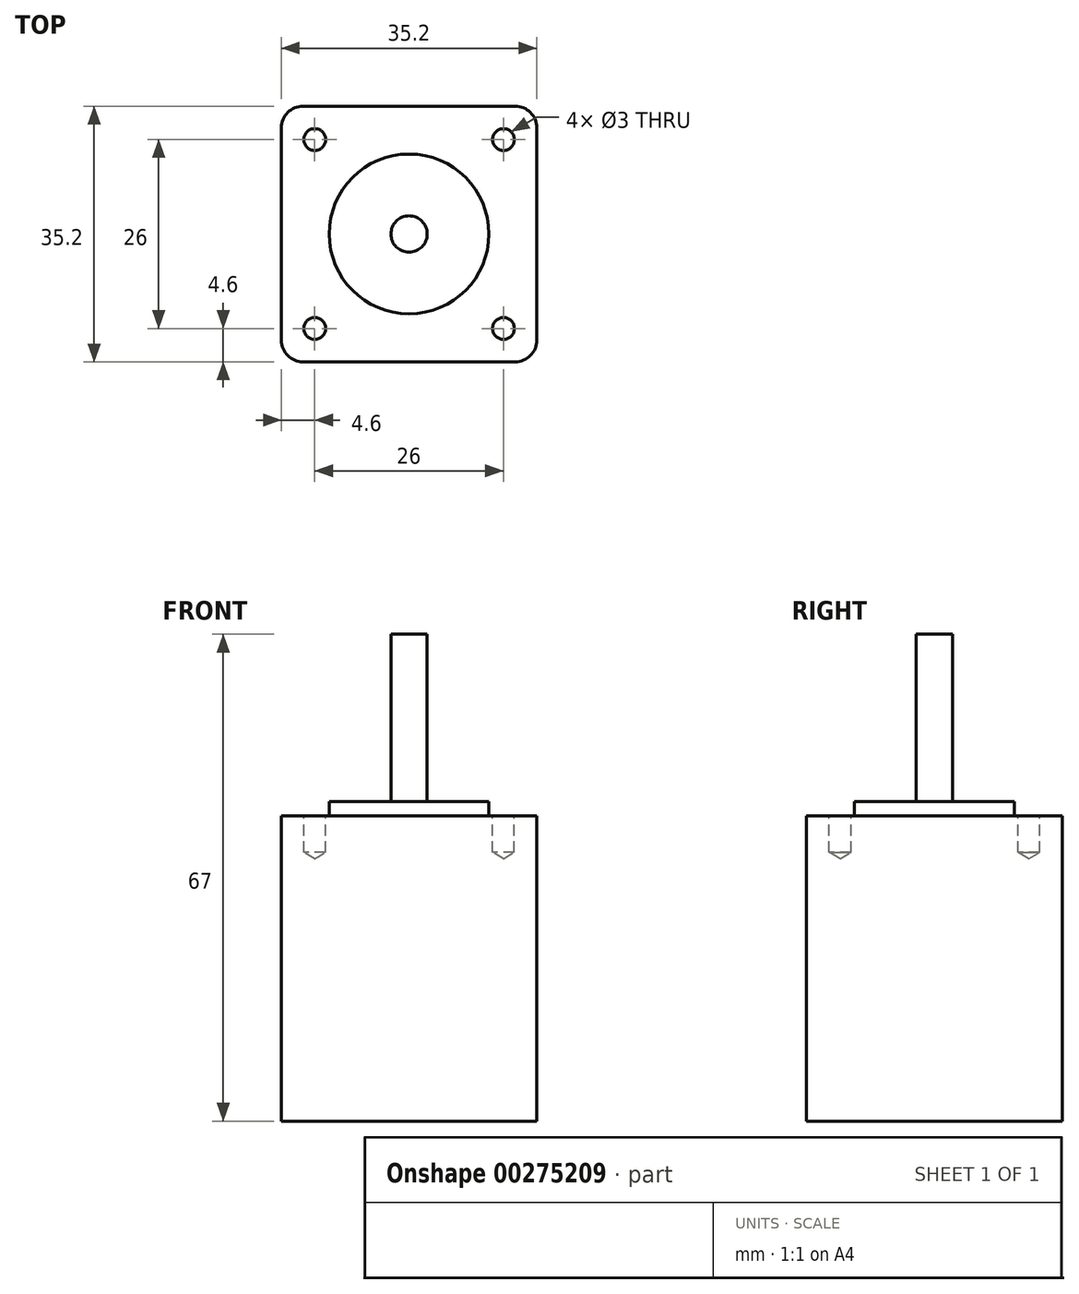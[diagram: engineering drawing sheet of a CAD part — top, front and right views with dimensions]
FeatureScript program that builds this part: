
annotation { "Feature Type Name" : "Feature", "Feature Type Description" : "" }
export const myFeature = defineFeature(function(context is Context, id is Id, definition is map)
    precondition{}
    {
        {
            var Q0;
            Q0=qCreatedBy(makeId("Top.planeOp"),FACE);
            var sketch = newSketch(context, id + "F0", { "sketchPlane" : qUnion([Q0])});
            skLineSegment(sketch, "E0.bottom", {"start": v(17.6, 17.6) * mm, "end": v(-17.6, 17.6) * mm});
            skLineSegment(sketch, "E0.top", {"start": v(17.6, -17.6) * mm, "end": v(-17.6, -17.6) * mm});
            skLineSegment(sketch, "E0.left", {"start": v(17.6, 17.6) * mm, "end": v(17.6, -17.6) * mm});
            skLineSegment(sketch, "E0.right", {"start": v(-17.6, 17.6) * mm, "end": v(-17.6, -17.6) * mm});
            skPoint(sketch, "E0.middle", {"position": v(0, 0) * mm});
            skCircle(sketch, "E1", {"center": v(0, 0) * mm, "radius": 11 * mm});
            skLineSegment(sketch, "E2.bottom", {"start": v(13, 13) * mm, "end": v(-13, 13) * mm});
            skLineSegment(sketch, "E2.top", {"start": v(13, -13) * mm, "end": v(-13, -13) * mm});
            skLineSegment(sketch, "E2.left", {"start": v(13, 13) * mm, "end": v(13, -13) * mm});
            skLineSegment(sketch, "E2.right", {"start": v(-13, 13) * mm, "end": v(-13, -13) * mm});
            skCircle(sketch, "E3", {"center": v(0, 0) * mm, "radius": 2.5 * mm});
            skPoint(sketch, "E4", {"position": v(-13, 13) * mm});
            skPoint(sketch, "E5", {"position": v(13, 13) * mm});
            skPoint(sketch, "E6", {"position": v(13, -13) * mm});
            skPoint(sketch, "E7", {"position": v(-13, -13) * mm});
            skSolve(sketch);
        }
        {
            var Q0;
            Q0=makeQuery(id+"F0.imprint","IMPRINT",FACE,{"disambiguationData":[TD([[makeQuery(id+"F0.imprint","IMPRINT",EDGE,{"derivedFrom":sQuery(id+"F0.wireOp",EDGE,"E0.bottom")}),1.0]])]});
            var Q1;
            Q1=makeQuery(id+"F0.imprint","IMPRINT",FACE,{"disambiguationData":[TD([[makeQuery(id+"F0.imprint","IMPRINT",EDGE,{"derivedFrom":sQuery(id+"F0.wireOp",EDGE,"E1")}),-1.0]])]});
            var Q2;
            Q2=makeQuery(id+"F0.imprint","IMPRINT",FACE,{"disambiguationData":[TD([[makeQuery(id+"F0.imprint","IMPRINT",EDGE,{"derivedFrom":sQuery(id+"F0.wireOp",EDGE,"E1")}),1.0]])]});
            var Q3;
            Q3=makeQuery(id+"F0.imprint","IMPRINT",FACE,{"disambiguationData":[TD([[makeQuery(id+"F0.imprint","IMPRINT",EDGE,{"derivedFrom":sQuery(id+"F0.wireOp",EDGE,"E3")}),1.0]])]});
            extrude(context, id + "F1", {"entities" : qUnion([Q0, Q1, Q2, Q3]), "oppositeDirection" : true, "depth" : 42 * mm});
        }
        {
            var Q0;
            Q0=makeQuery(id+"F0.imprint","IMPRINT",FACE,{"disambiguationData":[TD([[makeQuery(id+"F0.imprint","IMPRINT",EDGE,{"derivedFrom":sQuery(id+"F0.wireOp",EDGE,"E1")}),1.0]])]});
            extrude(context, id + "F2", {"entities" : qUnion([Q0]), "operationType" : NewBodyOperationType.ADD, "depth" : 2 * mm});
        }
        {
            var Q0;
            Q0=makeQuery(id+"F0.imprint","IMPRINT",FACE,{"disambiguationData":[TD([[makeQuery(id+"F0.imprint","IMPRINT",EDGE,{"derivedFrom":sQuery(id+"F0.wireOp",EDGE,"E3")}),1.0]])]});
            extrude(context, id + "F3", {"entities" : qUnion([Q0]), "operationType" : NewBodyOperationType.ADD, "depth" : 25 * mm});
        }
        {
            var Q0;
            Q0=makeQuery(id+"F1.opExtrude","SWEPT_EDGE",EDGE,{"disambiguationData":[OSD([sQuery(id+"F0.wireOp",EDGE,"E0.bottom"),sQuery(id+"F0.wireOp",EDGE,"E0.left")])]});
            var Q1;
            Q1=makeQuery(id+"F1.opExtrude","SWEPT_EDGE",EDGE,{"disambiguationData":[OSD([sQuery(id+"F0.wireOp",EDGE,"E0.top"),sQuery(id+"F0.wireOp",EDGE,"E0.left")])]});
            var Q2;
            Q2=makeQuery(id+"F1.opExtrude","SWEPT_EDGE",EDGE,{"disambiguationData":[OSD([sQuery(id+"F0.wireOp",EDGE,"E0.top"),sQuery(id+"F0.wireOp",EDGE,"E0.right")])]});
            var Q3;
            Q3=makeQuery(id+"F1.opExtrude","SWEPT_EDGE",EDGE,{"disambiguationData":[OSD([sQuery(id+"F0.wireOp",EDGE,"E0.bottom"),sQuery(id+"F0.wireOp",EDGE,"E0.right")])]});
            fillet(context, id + "F4", {"entities" : qUnion([Q0, Q1, Q2, Q3]), "radius" : 3 * mm, "tangentPropagation" : true, "allowEdgeOverflow" : false});
        }
        {
            var Q0;
            Q0=sQuery(id+"F0.wireOp",VERTEX,"E4");
            var Q1;
            Q1=sQuery(id+"F0.wireOp",VERTEX,"E5");
            var Q2;
            Q2=sQuery(id+"F0.wireOp",VERTEX,"E6");
            var Q3;
            Q3=sQuery(id+"F0.wireOp",VERTEX,"E7");
            var Q4;
            Q4=makeQuery(id+"F1.opExtrude","SWEPT_BODY",BODY,{"disambiguationData":[OSD([sQuery(id+"F0.wireOp",EDGE,"E0.bottom"),sQuery(id+"F0.wireOp",EDGE,"E0.top"),sQuery(id+"F0.wireOp",EDGE,"E0.left"),sQuery(id+"F0.wireOp",EDGE,"E0.right")])]});
            hole(context, id + "F5", {"style" : HoleStyle.SIMPLE, "endStyle" : HoleEndStyle.BLIND, "holeDiameter" : 3 * mm, "holeDepth" : 5 * mm, "tappedDepth" : 12 * mm, "tapClearance" : 3, "locations" : qUnion([Q0, Q1, Q2, Q3]), "scope" : qUnion([Q4])});
        }
    });
